# Revit family: 111213003058804
name_source: partatom
category: Modelos genéricos
revit_build: Autodesk Revit 2018 (Build: 20190510_1515(x64)
units: mm (PartAtom-declared; Revit-internal decimal feet)

## family parameters
Compartido = No
Corte con vacíos al cargar = No
Cota de conector redondo = Diámetro de uso
Puede alojar armadura = No
Punto de cálculo de habitación = No
Se basa en plano de trabajo = No
Siempre vertical = No
Tipo de pieza = Normal

## types (1)
- NARIZ DE GRADA PVC 37X37MM NEGRO TIRA 3.0MT
    Aplicacion = Escaleras
    Color = Negro
    Descripción = Nariz de grada PVC 37x37 MM
    Dimension = 37 mm  [stored 0.121391 ft]
    Dureza = 80 shore A
    Empresa = CNP SPA.
    Espesor = 2 mm  [stored 0.00656168 ft]
    Largo = 3000 mm  [stored 9.84252 ft]
    Material = PVC flexible negro
    Modelo = NARIZ DE GRADA PVC 37X37MM
    Nombre SKU = NARIZ DE GRADA PVC 37X37MM NEGRO TIRA 3.0MT
    Num SKUs = 111213003058804
    URL = https://www.empresascnp.cl
    Unidad = Tiras de 1.20 Mts y 3.00 Mts.
    Url Ficha tecnica = https://empresascnp.cl
    Uso = Se utiliza para instalarlos en los vértices de las escaleras hechas de cerámica, metal,
piso vinílico, entre otros. Con el objetivo de generar una solución antideslizante y así evitar
accidentes.
    Ventajas = Autoextinguible

note: [stored X ft] marks values corroborated as IEEE doubles in the binary element streams (Revit-internal decimal feet)

## geometry (parser evidence)
native form markers: Sweep x2
no freeform markers — native parametric forms only
